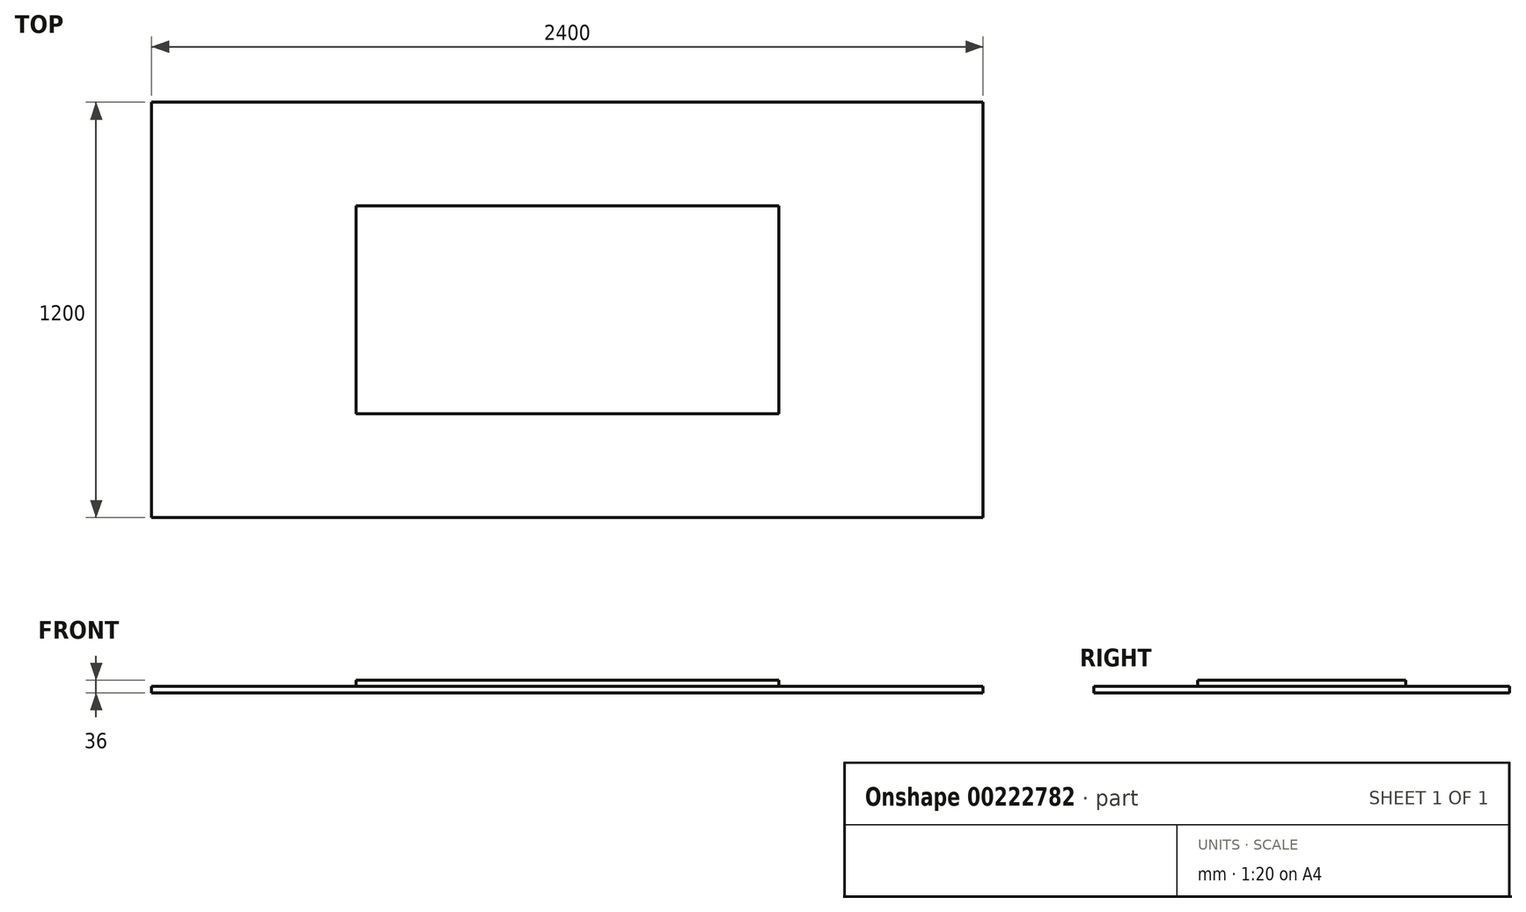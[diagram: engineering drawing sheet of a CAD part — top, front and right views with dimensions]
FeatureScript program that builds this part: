
annotation { "Feature Type Name" : "Feature", "Feature Type Description" : "" }
export const myFeature = defineFeature(function(context is Context, id is Id, definition is map)
    precondition{}
    {
        {
            var Q0;
            Q0=qCreatedBy(makeId("Top.planeOp"),FACE);
            var sketch = newSketch(context, id + "F0", { "sketchPlane" : qUnion([Q0])});
            skLineSegment(sketch, "E0.bottom", {"start": v(-590, 290) * mm, "end": v(590, 290) * mm, "construction": true});
            skLineSegment(sketch, "E0.top", {"start": v(-590, -290) * mm, "end": v(590, -290) * mm, "construction": true});
            skLineSegment(sketch, "E0.left", {"start": v(-590, 290) * mm, "end": v(-590, -290) * mm, "construction": true});
            skLineSegment(sketch, "E0.right", {"start": v(590, 290) * mm, "end": v(590, -290) * mm, "construction": true});
            skPoint(sketch, "E0.middle", {"position": v(0, 0) * mm});
            skLineSegment(sketch, "E1", {"start": v(0, 254.16) * mm, "end": v(0, -247.53) * mm, "construction": true});
            skLineSegment(sketch, "E2", {"start": v(-547.35, 0) * mm, "end": v(503.45, 0) * mm, "construction": true});
            skLineSegment(sketch, "E3.0", {"start": v(-610, 300) * mm, "end": v(610, 300) * mm});
            skLineSegment(sketch, "E3.2", {"start": v(-610, -300) * mm, "end": v(610, -300) * mm});
            skLineSegment(sketch, "E4", {"start": v(-610, 300) * mm, "end": v(-610, -300) * mm});
            skLineSegment(sketch, "E5.MirrorCS", {"start": v(610, 300) * mm, "end": v(610, -300) * mm});
            skSolve(sketch);
        }
        {
            var Q0;
            Q0=qSketchRegion(id+"F0",true);
            extrude(context, id + "F1", {"entities" : qUnion([Q0]), "depth" : 18 * mm});
        }
        {
            var Q0;
            Q0=qCreatedBy(makeId("Top.planeOp"),FACE);
            var sketch = newSketch(context, id + "F2", { "sketchPlane" : qUnion([Q0])});
            skLineSegment(sketch, "E6.bottom", {"start": v(-1200, 600) * mm, "end": v(1200, 600) * mm});
            skLineSegment(sketch, "E6.top", {"start": v(-1200, -600) * mm, "end": v(1200, -600) * mm});
            skLineSegment(sketch, "E6.left", {"start": v(-1200, 600) * mm, "end": v(-1200, -600) * mm});
            skLineSegment(sketch, "E6.right", {"start": v(1200, 600) * mm, "end": v(1200, -600) * mm});
            skPoint(sketch, "E6.middle", {"position": v(0, 0) * mm});
            skSolve(sketch);
        }
        {
            var Q0;
            Q0=qSketchRegion(id+"F2",true);
            extrude(context, id + "F3", {"entities" : qUnion([Q0]), "oppositeDirection" : true, "depth" : 18 * mm});
        }
    });
